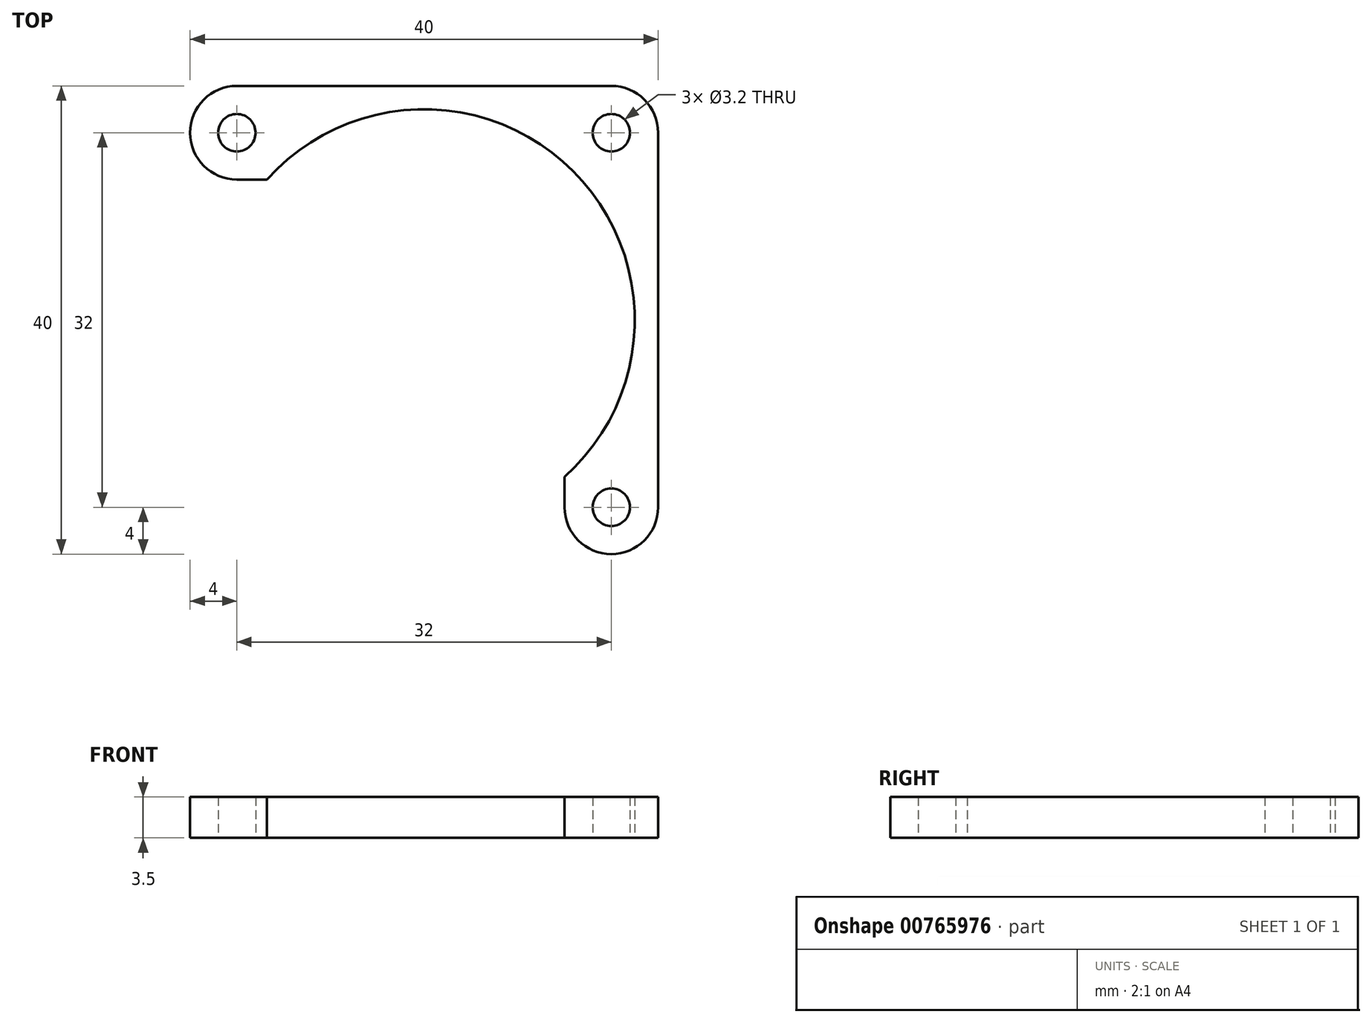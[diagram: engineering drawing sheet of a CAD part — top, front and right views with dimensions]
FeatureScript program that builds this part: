
annotation { "Feature Type Name" : "Feature", "Feature Type Description" : "" }
export const myFeature = defineFeature(function(context is Context, id is Id, definition is map)
    precondition{}
    {
        {
            var Q0;
            Q0=qCreatedBy(makeId("Top.planeOp"),FACE);
            var sketch = newSketch(context, id + "F0", { "sketchPlane" : qUnion([Q0])});
            skLineSegment(sketch, "E0.bottom", {"start": v(16, -16) * mm, "end": v(-16, -16) * mm, "construction": true});
            skLineSegment(sketch, "E0.top", {"start": v(16, 16) * mm, "end": v(-16, 16) * mm, "construction": true});
            skLineSegment(sketch, "E0.left", {"start": v(16, -16) * mm, "end": v(16, 16) * mm, "construction": true});
            skLineSegment(sketch, "E0.right", {"start": v(-16, -16) * mm, "end": v(-16, 16) * mm, "construction": true});
            skPoint(sketch, "E0.middle", {"position": v(0, 0) * mm});
            skCircle(sketch, "E1", {"center": v(-16, 16) * mm, "radius": 1.6 * mm});
            skCircle(sketch, "E2", {"center": v(16, 16) * mm, "radius": 1.6 * mm});
            skCircle(sketch, "E3", {"center": v(16, -16) * mm, "radius": 1.6 * mm});
            skArc(sketch, "E4", {"start": v(-16, 20) * mm, "mid": v(-20, 16) * mm, "end": v(-16, 12) * mm});
            skArc(sketch, "E5", {"start": v(12, -16) * mm, "mid": v(16, -20) * mm, "end": v(20, -16) * mm});
            skArc(sketch, "E6", {"start": v(16, 20) * mm, "mid": v(18.83, 18.83) * mm, "end": v(20, 16) * mm});
            skLineSegment(sketch, "E7", {"start": v(-16, 20) * mm, "end": v(16, 20) * mm});
            skLineSegment(sketch, "E8", {"start": v(20, 16) * mm, "end": v(20, -16) * mm});
            skLineSegment(sketch, "E9", {"start": v(-16, 12) * mm, "end": v(-13.42, 12) * mm});
            skLineSegment(sketch, "E10", {"start": v(12, -16) * mm, "end": v(12, -13.42) * mm});
            skArc(sketch, "E11", {"start": v(-13.42, 12) * mm, "mid": v(12.73, 12.73) * mm, "end": v(12, -13.42) * mm});
            skSolve(sketch);
        }
        {
            var Q0;
            Q0 = qSketchRegion(id + "F0", true);
            extrude(context, id + "F1", {"entities" : qUnion([Q0]), "depth" : 3.5 * mm, "offsetDistance" : 25 * mm});
        }
    });
